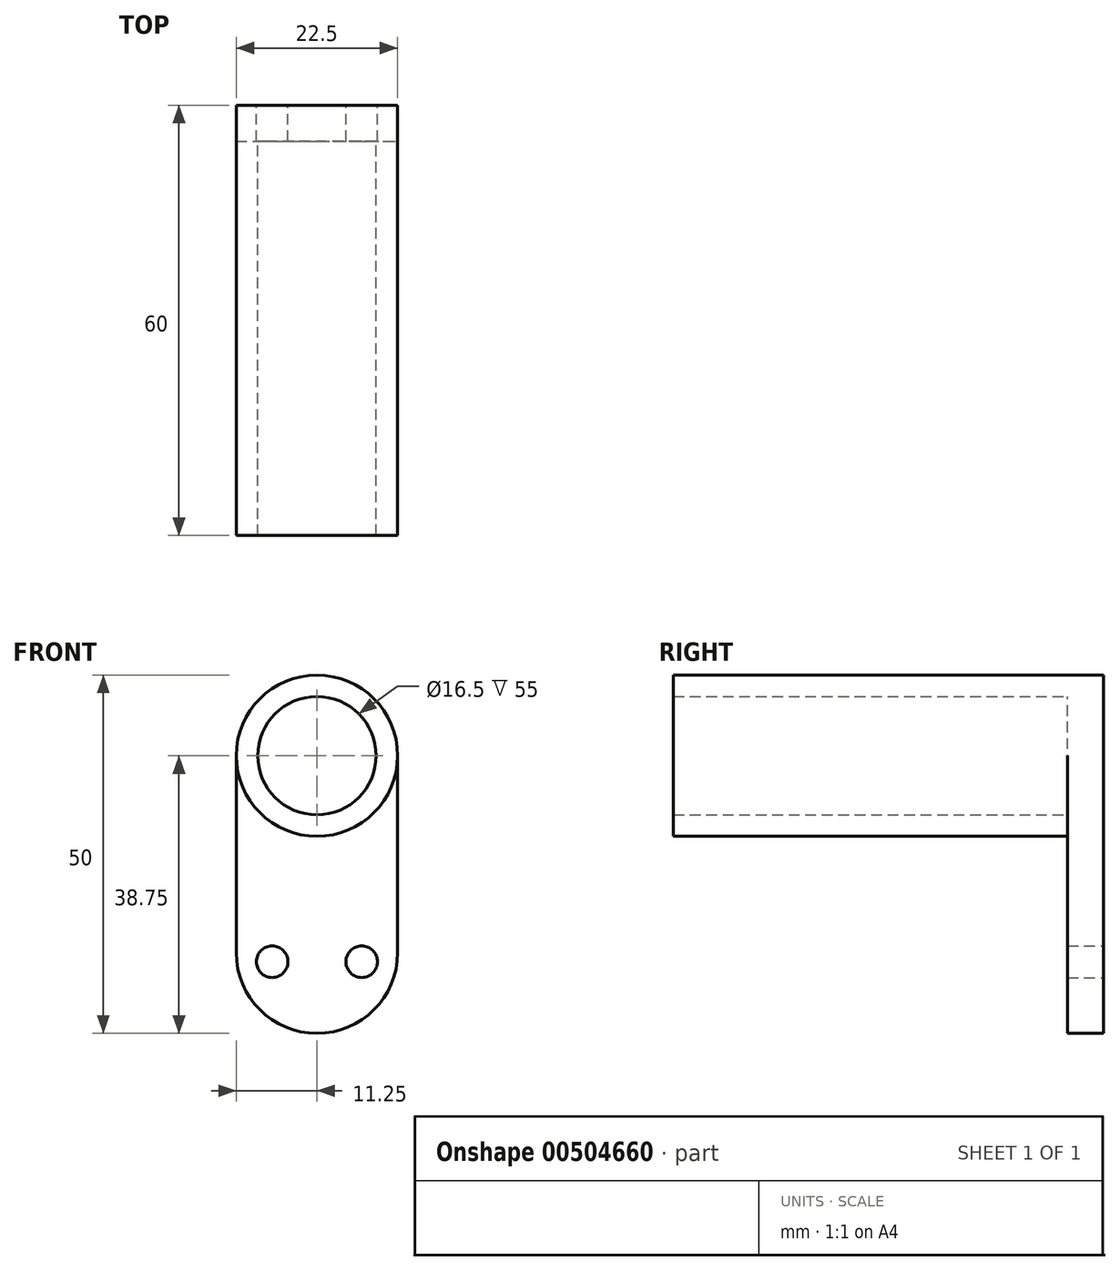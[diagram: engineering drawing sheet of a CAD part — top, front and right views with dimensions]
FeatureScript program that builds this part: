
annotation { "Feature Type Name" : "Feature", "Feature Type Description" : "" }
export const myFeature = defineFeature(function(context is Context, id is Id, definition is map)
    precondition{}
    {
        {
            var Q0;
            Q0=qCreatedBy(makeId("Front.planeOp"),FACE);
            var sketch = newSketch(context, id + "F0", { "sketchPlane" : qUnion([Q0])});
            skLineSegment(sketch, "E0.bottom", {"start": v(0, 0) * mm, "end": v(22.5, 0) * mm});
            skLineSegment(sketch, "E0.top", {"start": v(0, 50) * mm, "end": v(22.5, 50) * mm});
            skLineSegment(sketch, "E0.left", {"start": v(0, 0) * mm, "end": v(0, 50) * mm});
            skLineSegment(sketch, "E0.right", {"start": v(22.5, 0) * mm, "end": v(22.5, 50) * mm});
            skLineSegment(sketch, "E1", {"start": v(0, 10) * mm, "end": v(22.5, 10) * mm, "construction": true});
            skPoint(sketch, "E2", {"position": v(5, 10) * mm});
            skPoint(sketch, "E3", {"position": v(17.5, 10) * mm});
            skSolve(sketch);
        }
        {
            var Q0;
            Q0 = qSketchRegion(id + "F0", true);
            extrude(context, id + "F1", {"entities" : qUnion([Q0]), "depth" : 5 * mm});
        }
        {
            var Q0;
            Q0=sQuery(id+"F0.wireOp",VERTEX,"E2");
            var Q1;
            Q1=sQuery(id+"F0.wireOp",VERTEX,"E3");
            var Q2;
            Q2=makeQuery(id+"F1.opExtrude","SWEPT_BODY",BODY,{"disambiguationData":[OSD([sQuery(id+"F0.wireOp",EDGE,"E0.bottom"),sQuery(id+"F0.wireOp",EDGE,"E0.top"),sQuery(id+"F0.wireOp",EDGE,"E0.left"),sQuery(id+"F0.wireOp",EDGE,"E0.right")])]});
            hole(context, id + "F2", {"style" : HoleStyle.SIMPLE, "endStyle" : HoleEndStyle.THROUGH, "oppositeDirection" : true, "standardTappedOrClearance" : lookupTablePath({ "standard" : "ISO", "fit" : "Normal", "size" : "M4", "type" : "Clearance" }), "standardBlindInLast" : lookupTablePath({ "fit" : "Standard", "standard" : "ISO", "size" : "M4", "type" : "Clearance" }), "holeDiameter" : 4.4 * mm, "isTappedThrough" : true, "tappedDepth" : 12 * mm, "tapClearance" : 3, "locations" : qUnion([Q0, Q1]), "scope" : qUnion([Q2])});
        }
        {
            var Q0;
            Q0=makeQuery(id+"F1.opExtrude","CAP_FACE",FACE,{"disambiguationData":[OSD([sQuery(id+"F0.wireOp",EDGE,"E0.bottom"),sQuery(id+"F0.wireOp",EDGE,"E0.top"),sQuery(id+"F0.wireOp",EDGE,"E0.left"),sQuery(id+"F0.wireOp",EDGE,"E0.right")])],"isStart":false});
            var sketch = newSketch(context, id + "F3", { "sketchPlane" : qUnion([Q0])});
            skCircle(sketch, "E4", {"center": v(11.25, 38.75) * mm, "radius": 11.25 * mm});
            skCircle(sketch, "E5", {"center": v(11.25, 38.75) * mm, "radius": 8.25 * mm});
            skSolve(sketch);
        }
        {
            var Q0;
            Q0=makeQuery(id+"F1.opExtrude","SWEPT_EDGE",EDGE,{"disambiguationData":[OSD([sQuery(id+"F0.wireOp",EDGE,"E0.top"),sQuery(id+"F0.wireOp",EDGE,"E0.right")])]});
            var Q1;
            Q1=makeQuery(id+"F1.opExtrude","SWEPT_EDGE",EDGE,{"disambiguationData":[OSD([sQuery(id+"F0.wireOp",EDGE,"E0.top"),sQuery(id+"F0.wireOp",EDGE,"E0.left")])]});
            var Q2;
            Q2=makeQuery(id+"F1.opExtrude","SWEPT_EDGE",EDGE,{"disambiguationData":[OSD([sQuery(id+"F0.wireOp",EDGE,"E0.bottom"),sQuery(id+"F0.wireOp",EDGE,"E0.right")])]});
            var Q3;
            Q3=makeQuery(id+"F1.opExtrude","SWEPT_EDGE",EDGE,{"disambiguationData":[OSD([sQuery(id+"F0.wireOp",EDGE,"E0.bottom"),sQuery(id+"F0.wireOp",EDGE,"E0.left")])]});
            fillet(context, id + "F4", {"entities" : qUnion([Q0, Q1, Q2, Q3]), "radius" : (22.5 / 2) * mm, "tangentPropagation" : true, "allowEdgeOverflow" : false});
        }
        {
            var Q0;
            Q0 = qSketchRegion(id + "F3", true);
            extrude(context, id + "F5", {"entities" : qUnion([Q0]), "operationType" : NewBodyOperationType.ADD, "depth" : 55 * mm});
        }
    });
